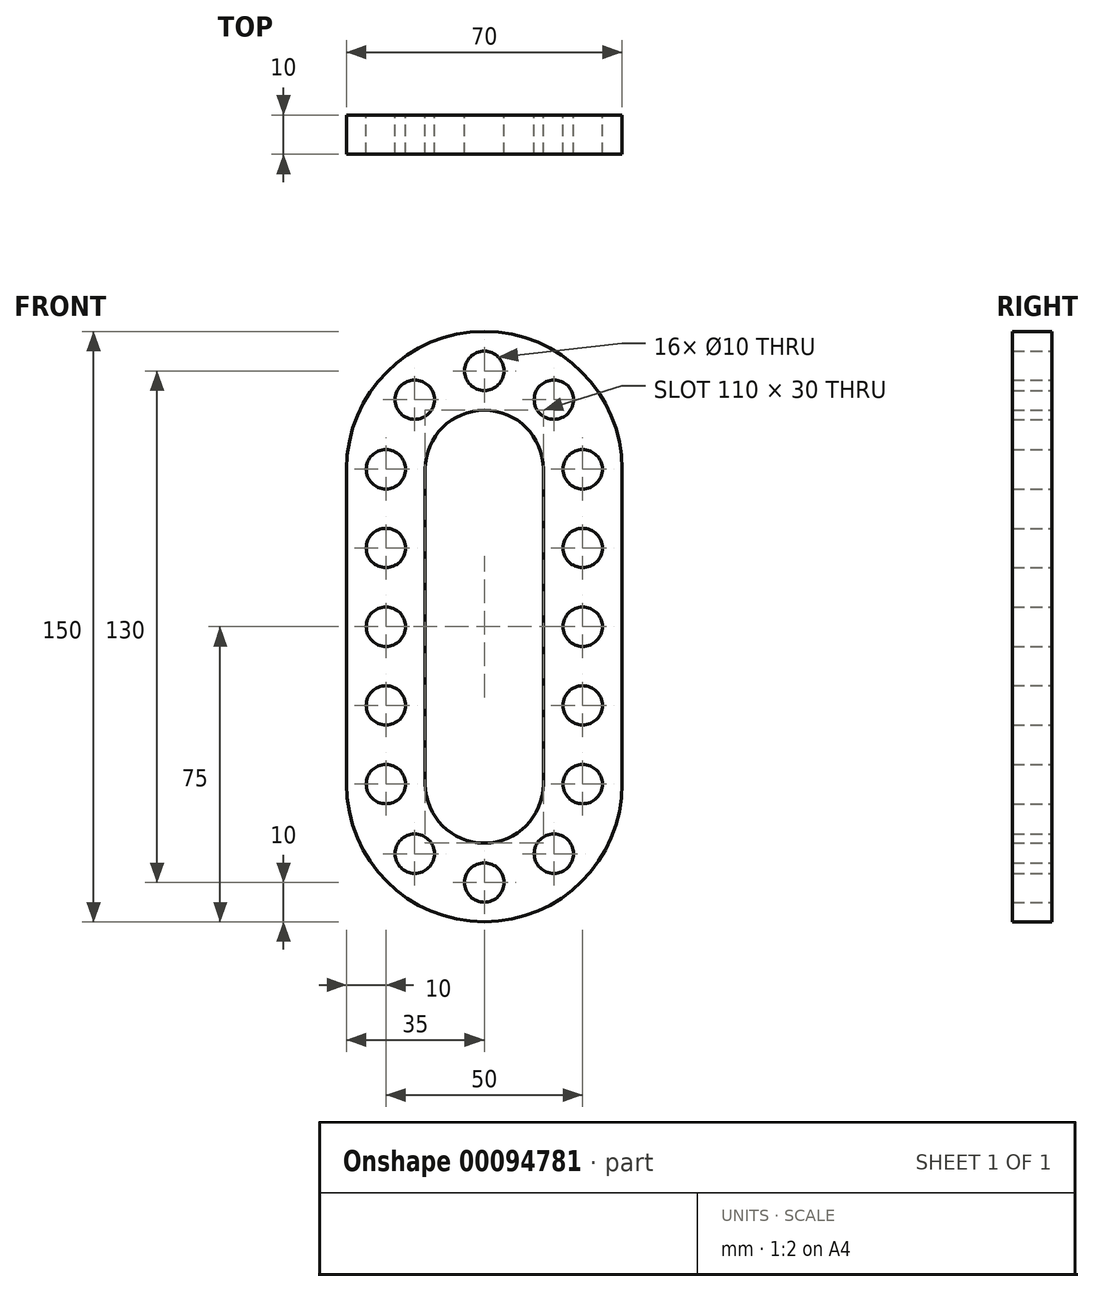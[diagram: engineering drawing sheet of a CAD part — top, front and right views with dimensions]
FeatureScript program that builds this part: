
annotation { "Feature Type Name" : "Feature", "Feature Type Description" : "" }
export const myFeature = defineFeature(function(context is Context, id is Id, definition is map)
    precondition{}
    {
        {
            var Q0;
            Q0=qCreatedBy(makeId("Front.planeOp"),FACE);
            var sketch = newSketch(context, id + "F0", { "sketchPlane" : qUnion([Q0])});
            skArc(sketch, "E0", {"start": v(0, 55) * mm, "mid": v(-10.6, 50.6) * mm, "end": v(-15, 40) * mm});
            skLineSegment(sketch, "E1", {"start": v(-15, 40) * mm, "end": v(-15, 0) * mm});
            skLineSegment(sketch, "E2.0", {"start": v(-35, 40) * mm, "end": v(-35, 0) * mm});
            skArc(sketch, "E2.1", {"start": v(0, 75) * mm, "mid": v(-24.75, 64.75) * mm, "end": v(-35, 40) * mm});
            skLineSegment(sketch, "E3", {"start": v(-35, 40) * mm, "end": v(43.7, 40) * mm, "construction": true});
            skCircle(sketch, "E4", {"center": v(-25, 40) * mm, "radius": 5 * mm});
            skCircle(sketch, "E5.1.0", {"center": v(-17.68, 57.68) * mm, "radius": 5 * mm});
            skCircle(sketch, "E5.2.0", {"center": v(0, 65) * mm, "radius": 5 * mm});
            skLineSegment(sketch, "E5.anchor1", {"start": v(0, 40) * mm, "end": v(-25, 40) * mm, "construction": true});
            skLineSegment(sketch, "E5.anchor2", {"start": v(0, 40) * mm, "end": v(0, 65) * mm, "construction": true});
            skCircle(sketch, "E6", {"center": v(-25, 0) * mm, "radius": 5 * mm});
            skCircle(sketch, "E7", {"center": v(-25, 20) * mm, "radius": 5 * mm});
            skLineSegment(sketch, "E8.MirrorCS", {"start": v(15, 40) * mm, "end": v(15, 0) * mm});
            skLineSegment(sketch, "E9.MirrorCS", {"start": v(35, 40) * mm, "end": v(35, 0) * mm});
            skCircle(sketch, "E10.MirrorC", {"center": v(25, 20) * mm, "radius": 5 * mm});
            skCircle(sketch, "E11.MirrorC", {"center": v(25, 40) * mm, "radius": 5 * mm});
            skCircle(sketch, "E12.MirrorC", {"center": v(17.68, 57.68) * mm, "radius": 5 * mm});
            skArc(sketch, "E13.MirrorCS", {"start": v(0, 55) * mm, "mid": v(10.6, 50.6) * mm, "end": v(15, 40) * mm});
            skArc(sketch, "E14.MirrorCS", {"start": v(0, 75) * mm, "mid": v(24.75, 64.75) * mm, "end": v(35, 40) * mm});
            skCircle(sketch, "E15.MirrorC", {"center": v(25, 0) * mm, "radius": 5 * mm});
            skLineSegment(sketch, "E16.MirrorCS", {"start": v(-15, -40) * mm, "end": v(-15, 0) * mm});
            skLineSegment(sketch, "E17.MirrorCS", {"start": v(-35, -40) * mm, "end": v(-35, 0) * mm});
            skCircle(sketch, "E18.MirrorC", {"center": v(-25, -20) * mm, "radius": 5 * mm});
            skCircle(sketch, "E19.MirrorC", {"center": v(-25, -40) * mm, "radius": 5 * mm});
            skCircle(sketch, "E20.MirrorC", {"center": v(-17.68, -57.68) * mm, "radius": 5 * mm});
            skCircle(sketch, "E21.MirrorC", {"center": v(0, -65) * mm, "radius": 5 * mm});
            skArc(sketch, "E22.MirrorCS", {"start": v(0, -55) * mm, "mid": v(-10.6, -50.6) * mm, "end": v(-15, -40) * mm});
            skArc(sketch, "E23.MirrorCS", {"start": v(0, -75) * mm, "mid": v(-24.75, -64.75) * mm, "end": v(-35, -40) * mm});
            skArc(sketch, "E24.MirrorCS", {"start": v(0, -55) * mm, "mid": v(10.6, -50.6) * mm, "end": v(15, -40) * mm});
            skLineSegment(sketch, "E25.MirrorCS", {"start": v(15, -40) * mm, "end": v(15, 0) * mm});
            skLineSegment(sketch, "E26.MirrorCS", {"start": v(35, -40) * mm, "end": v(35, 0) * mm});
            skCircle(sketch, "E27.MirrorC", {"center": v(25, -20) * mm, "radius": 5 * mm});
            skCircle(sketch, "E28.MirrorC", {"center": v(25, -40) * mm, "radius": 5 * mm});
            skCircle(sketch, "E29.MirrorC", {"center": v(17.68, -57.68) * mm, "radius": 5 * mm});
            skArc(sketch, "E30.MirrorCS", {"start": v(0, -75) * mm, "mid": v(24.75, -64.75) * mm, "end": v(35, -40) * mm});
            skSolve(sketch);
        }
        {
            var Q0;
            Q0 = qSketchRegion(id + "F0", true);
            extrude(context, id + "F1", {"entities" : qUnion([Q0]), "depth" : 10 * mm});
        }
    });
